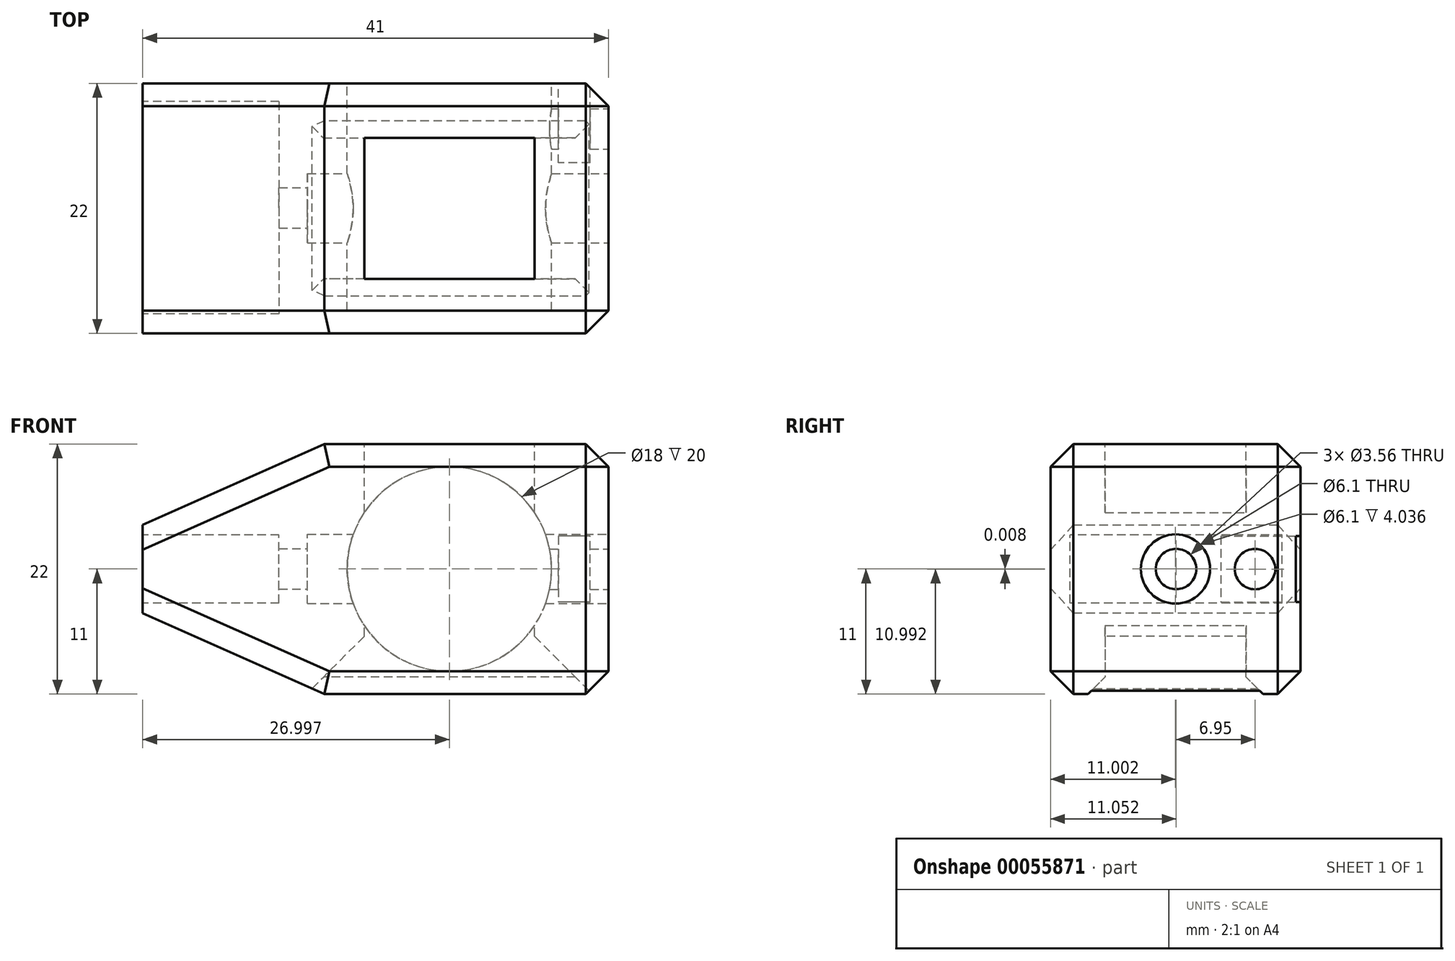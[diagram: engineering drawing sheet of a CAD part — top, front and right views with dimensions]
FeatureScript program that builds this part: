
annotation { "Feature Type Name" : "Feature", "Feature Type Description" : "" }
export const myFeature = defineFeature(function(context is Context, id is Id, definition is map)
    precondition{}
    {
        {
            var Q0;
            Q0=qCreatedBy(makeId("Top.planeOp"),FACE);
            var sketch = newSketch(context, id + "F0", { "sketchPlane" : qUnion([Q0])});
            skLineSegment(sketch, "E0.bottom", {"start": v(-13.98, 8.23) * mm, "end": v(12.02, 8.23) * mm});
            skLineSegment(sketch, "E0.top", {"start": v(-13.98, -13.77) * mm, "end": v(12.02, -13.77) * mm});
            skLineSegment(sketch, "E0.left", {"start": v(-13.98, 8.23) * mm, "end": v(-13.98, -13.77) * mm});
            skLineSegment(sketch, "E0.right", {"start": v(12.02, 8.23) * mm, "end": v(12.02, -13.77) * mm});
            skSolve(sketch);
        }
        {
            var Q0;
            Q0=qSketchRegion(id+"F0",true);
            extrude(context, id + "F1", {"entities" : qUnion([Q0]), "depth" : 22 * mm});
        }
        {
            var Q0;
            Q0=makeQuery(id+"F1.opExtrude","SWEPT_FACE",FACE,{"disambiguationData":[OSD([sQuery(id+"F0.wireOp",EDGE,"E0.bottom")])]});
            var sketch = newSketch(context, id + "F2", { "sketchPlane" : qUnion([Q0])});
            skCircle(sketch, "E1", {"center": v(0.98, 11) * mm, "radius": 9 * mm});
            skSolve(sketch);
        }
        {
            var Q0;
            Q0=qSketchRegion(id+"F2",true);
            extrude(context, id + "F3", {"entities" : qUnion([Q0]), "operationType" : NewBodyOperationType.REMOVE, "oppositeDirection" : true, "depth" : 20 * mm});
        }
        {
            var Q0;
            Q0=makeQuery(id+"F1.opExtrude","CAP_FACE",FACE,{"disambiguationData":[OSD([sQuery(id+"F0.wireOp",EDGE,"E0.bottom"),sQuery(id+"F0.wireOp",EDGE,"E0.top"),sQuery(id+"F0.wireOp",EDGE,"E0.left"),sQuery(id+"F0.wireOp",EDGE,"E0.right")])],"isStart":false});
            var sketch = newSketch(context, id + "F4", { "sketchPlane" : qUnion([Q0])});
            skLineSegment(sketch, "E2.bottom", {"start": v(-8.48, 3.43) * mm, "end": v(6.52, 3.43) * mm});
            skLineSegment(sketch, "E2.top", {"start": v(-8.48, -8.97) * mm, "end": v(6.52, -8.97) * mm});
            skLineSegment(sketch, "E2.left", {"start": v(-8.48, 3.43) * mm, "end": v(-8.48, -8.97) * mm});
            skLineSegment(sketch, "E2.right", {"start": v(6.52, 3.43) * mm, "end": v(6.52, -8.97) * mm});
            skSolve(sketch);
        }
        {
            var Q0;
            Q0=qSketchRegion(id+"F4",true);
            extrude(context, id + "F5", {"entities" : qUnion([Q0]), "operationType" : NewBodyOperationType.REMOVE, "endBound" : BoundingType.THROUGH_ALL, "oppositeDirection" : true, "depth" : 10 * mm});
        }
        {
            var Q0;
            Q0=makeQuery(id+"F1.opExtrude","SWEPT_FACE",FACE,{"disambiguationData":[OSD([sQuery(id+"F0.wireOp",EDGE,"E0.left")])]});
            var sketch = newSketch(context, id + "F6", { "sketchPlane" : qUnion([Q0])});
            skLineSegment(sketch, "E3.bottom", {"start": v(-8.23, 22) * mm, "end": v(13.77, 22) * mm});
            skLineSegment(sketch, "E3.top", {"start": v(-8.23, 0) * mm, "end": v(13.77, 0) * mm});
            skLineSegment(sketch, "E3.left", {"start": v(-8.23, 22) * mm, "end": v(-8.23, 0) * mm});
            skLineSegment(sketch, "E3.right", {"start": v(13.77, 22) * mm, "end": v(13.77, 0) * mm});
            skSolve(sketch);
        }
        {
            var Q0;
            Q0=qSketchRegion(id+"F6",true);
            extrude(context, id + "F7", {"entities" : qUnion([Q0]), "operationType" : NewBodyOperationType.ADD, "depth" : 14 * mm});
        }
        {
            var Q0;
            Q0=makeQuery(id+"F7.opExtrude","CAP_FACE",FACE,{"disambiguationData":[OSD([sQuery(id+"F6.wireOp",EDGE,"E3.bottom"),sQuery(id+"F6.wireOp",EDGE,"E3.top"),sQuery(id+"F6.wireOp",EDGE,"E3.left"),sQuery(id+"F6.wireOp",EDGE,"E3.right")])],"isStart":false});
            var sketch = newSketch(context, id + "F8", { "sketchPlane" : qUnion([Q0])});
            skLineSegment(sketch, "E4.bottom", {"start": v(-6.63, 8) * mm, "end": v(12.07, 8) * mm});
            skLineSegment(sketch, "E4.top", {"start": v(-6.63, 14) * mm, "end": v(12.07, 14) * mm});
            skLineSegment(sketch, "E4.left", {"start": v(-6.63, 8) * mm, "end": v(-6.63, 14) * mm});
            skLineSegment(sketch, "E4.right", {"start": v(12.07, 8) * mm, "end": v(12.07, 14) * mm});
            skSolve(sketch);
        }
        {
            var Q0;
            Q0=qSketchRegion(id+"F8",true);
            extrude(context, id + "F9", {"entities" : qUnion([Q0]), "operationType" : NewBodyOperationType.REMOVE, "oppositeDirection" : true, "depth" : 12 * mm});
        }
        {
            var Q0;
            Q0=makeQuery(id+"F1.opExtrude","SWEPT_FACE",FACE,{"disambiguationData":[OSD([sQuery(id+"F0.wireOp",EDGE,"E0.right")])]});
            var sketch = newSketch(context, id + "F10", { "sketchPlane" : qUnion([Q0])});
            skCircle(sketch, "E5", {"center": v(-2.72, 11) * mm, "radius": 1.78 * mm});
            skSolve(sketch);
        }
        {
            var Q0;
            Q0=qSketchRegion(id+"F10",true);
            extrude(context, id + "F11", {"entities" : qUnion([Q0]), "operationType" : NewBodyOperationType.REMOVE, "endBound" : BoundingType.THROUGH_ALL, "oppositeDirection" : true, "depth" : 25.4 * mm});
        }
        {
            var Q0;
            Q0=makeQuery(id+"F5.boolean.opBoolean","COPY",EDGE,{"derivedFrom":makeQuery(id+"F5.opExtrude","CAP_EDGE",EDGE,{"disambiguationData":[OSD([sQuery(id+"F4.wireOp",EDGE,"E2.bottom")])],"isStart":true})});
            var Q1;
            Q1=makeQuery(id+"F5.boolean.opBoolean","COPY",EDGE,{"derivedFrom":makeQuery(id+"F5.opExtrude","CAP_EDGE",EDGE,{"disambiguationData":[OSD([sQuery(id+"F4.wireOp",EDGE,"E2.top")])],"isStart":true})});
            var Q2;
            Q2=makeQuery(id+"F5.boolean.opBoolean","INTERSECT",EDGE,{"derivedFrom":[makeQuery(id+"F1.opExtrude","CAP_FACE",FACE,{"disambiguationData":[OSD([sQuery(id+"F0.wireOp",EDGE,"E0.bottom"),sQuery(id+"F0.wireOp",EDGE,"E0.top"),sQuery(id+"F0.wireOp",EDGE,"E0.left"),sQuery(id+"F0.wireOp",EDGE,"E0.right")])],"isStart":true}),makeQuery(id+"F5.opExtrude","SWEPT_FACE",FACE,{"disambiguationData":[OSD([sQuery(id+"F4.wireOp",EDGE,"E2.bottom")])]})]});
            var Q3;
            Q3=makeQuery(id+"F5.boolean.opBoolean","INTERSECT",EDGE,{"derivedFrom":[makeQuery(id+"F1.opExtrude","CAP_FACE",FACE,{"disambiguationData":[OSD([sQuery(id+"F0.wireOp",EDGE,"E0.bottom"),sQuery(id+"F0.wireOp",EDGE,"E0.top"),sQuery(id+"F0.wireOp",EDGE,"E0.left"),sQuery(id+"F0.wireOp",EDGE,"E0.right")])],"isStart":true}),makeQuery(id+"F5.opExtrude","SWEPT_FACE",FACE,{"disambiguationData":[OSD([sQuery(id+"F4.wireOp",EDGE,"E2.top")])]})]});
            chamfer(context, id + "F12", {"entities" : qUnion([Q0, Q1, Q2, Q3]), "width" : 1.5 * mm, "tangentPropagation" : true});
        }
        {
            var Q0;
            Q0=makeQuery(id+"F7.opExtrude","CAP_EDGE",EDGE,{"disambiguationData":[OSD([sQuery(id+"F6.wireOp",EDGE,"E3.bottom")])],"isStart":false});
            var Q1;
            Q1=makeQuery(id+"F7.opExtrude","CAP_EDGE",EDGE,{"disambiguationData":[OSD([sQuery(id+"F6.wireOp",EDGE,"E3.top")])],"isStart":false});
            chamfer(context, id + "F13", {"entities" : qUnion([Q0, Q1]), "chamferType" : ChamferType.OFFSET_ANGLE, "width" : 16 * mm, "oppositeDirection" : false, "angle" : 24 * degree, "tangentPropagation" : true});
        }
        {
            var Q0;
            Q0=makeQuery(id+"F13.opChamfer","BLEND_EDGE",EDGE,{"blendedFrom":[makeQuery(id+"F7.opExtrude","CAP_EDGE",EDGE,{"disambiguationData":[OSD([sQuery(id+"F6.wireOp",EDGE,"E3.bottom")])],"isStart":false}),makeQuery(id+"F7.boolean.opBoolean","MERGE",FACE,{"derivedFrom":[makeQuery(id+"F1.opExtrude","SWEPT_FACE",FACE,{"disambiguationData":[OSD([sQuery(id+"F0.wireOp",EDGE,"E0.bottom")])]}),makeQuery(id+"F7.opExtrude","SWEPT_FACE",FACE,{"disambiguationData":[OSD([sQuery(id+"F6.wireOp",EDGE,"E3.left")])]})]})],"blendedInto":[makeQuery(id+"F7.boolean.opBoolean","MERGE",FACE,{"derivedFrom":[makeQuery(id+"F1.opExtrude","SWEPT_FACE",FACE,{"disambiguationData":[OSD([sQuery(id+"F0.wireOp",EDGE,"E0.bottom")])]}),makeQuery(id+"F7.opExtrude","SWEPT_FACE",FACE,{"disambiguationData":[OSD([sQuery(id+"F6.wireOp",EDGE,"E3.left")])]})]})]});
            var Q1;
            Q1=makeQuery(id+"F13.opChamfer","BLEND_EDGE",EDGE,{"blendedFrom":[makeQuery(id+"F7.opExtrude","CAP_EDGE",EDGE,{"disambiguationData":[OSD([sQuery(id+"F6.wireOp",EDGE,"E3.bottom")])],"isStart":false}),makeQuery(id+"F7.boolean.opBoolean","MERGE",FACE,{"derivedFrom":[makeQuery(id+"F1.opExtrude","SWEPT_FACE",FACE,{"disambiguationData":[OSD([sQuery(id+"F0.wireOp",EDGE,"E0.top")])]}),makeQuery(id+"F7.opExtrude","SWEPT_FACE",FACE,{"disambiguationData":[OSD([sQuery(id+"F6.wireOp",EDGE,"E3.right")])]})]})],"blendedInto":[makeQuery(id+"F7.boolean.opBoolean","MERGE",FACE,{"derivedFrom":[makeQuery(id+"F1.opExtrude","SWEPT_FACE",FACE,{"disambiguationData":[OSD([sQuery(id+"F0.wireOp",EDGE,"E0.top")])]}),makeQuery(id+"F7.opExtrude","SWEPT_FACE",FACE,{"disambiguationData":[OSD([sQuery(id+"F6.wireOp",EDGE,"E3.right")])]})]})]});
            var Q2;
            Q2=makeQuery(id+"F13.opChamfer","BLEND_EDGE",EDGE,{"blendedFrom":[makeQuery(id+"F7.opExtrude","CAP_EDGE",EDGE,{"disambiguationData":[OSD([sQuery(id+"F6.wireOp",EDGE,"E3.top")])],"isStart":false}),makeQuery(id+"F7.boolean.opBoolean","MERGE",FACE,{"derivedFrom":[makeQuery(id+"F1.opExtrude","SWEPT_FACE",FACE,{"disambiguationData":[OSD([sQuery(id+"F0.wireOp",EDGE,"E0.bottom")])]}),makeQuery(id+"F7.opExtrude","SWEPT_FACE",FACE,{"disambiguationData":[OSD([sQuery(id+"F6.wireOp",EDGE,"E3.left")])]})]})],"blendedInto":[makeQuery(id+"F7.boolean.opBoolean","MERGE",FACE,{"derivedFrom":[makeQuery(id+"F1.opExtrude","SWEPT_FACE",FACE,{"disambiguationData":[OSD([sQuery(id+"F0.wireOp",EDGE,"E0.bottom")])]}),makeQuery(id+"F7.opExtrude","SWEPT_FACE",FACE,{"disambiguationData":[OSD([sQuery(id+"F6.wireOp",EDGE,"E3.left")])]})]})]});
            var Q3;
            Q3=makeQuery(id+"F13.opChamfer","BLEND_EDGE",EDGE,{"blendedFrom":[makeQuery(id+"F7.opExtrude","CAP_EDGE",EDGE,{"disambiguationData":[OSD([sQuery(id+"F6.wireOp",EDGE,"E3.top")])],"isStart":false}),makeQuery(id+"F7.boolean.opBoolean","MERGE",FACE,{"derivedFrom":[makeQuery(id+"F1.opExtrude","SWEPT_FACE",FACE,{"disambiguationData":[OSD([sQuery(id+"F0.wireOp",EDGE,"E0.top")])]}),makeQuery(id+"F7.opExtrude","SWEPT_FACE",FACE,{"disambiguationData":[OSD([sQuery(id+"F6.wireOp",EDGE,"E3.right")])]})]})],"blendedInto":[makeQuery(id+"F7.boolean.opBoolean","MERGE",FACE,{"derivedFrom":[makeQuery(id+"F1.opExtrude","SWEPT_FACE",FACE,{"disambiguationData":[OSD([sQuery(id+"F0.wireOp",EDGE,"E0.top")])]}),makeQuery(id+"F7.opExtrude","SWEPT_FACE",FACE,{"disambiguationData":[OSD([sQuery(id+"F6.wireOp",EDGE,"E3.right")])]})]})]});
            chamfer(context, id + "F14", {"entities" : qUnion([Q0, Q1, Q2, Q3]), "width" : 2 * mm, "tangentPropagation" : true});
        }
        {
            var Q0;
            Q0=makeQuery(id+"F14.opChamfer","SPLIT",FACE,{"disambiguationData":[OD(0.0)],"derivedFrom":makeQuery(id+"F7.boolean.opBoolean","MERGE",FACE,{"derivedFrom":[makeQuery(id+"F1.opExtrude","SWEPT_FACE",FACE,{"disambiguationData":[OSD([sQuery(id+"F0.wireOp",EDGE,"E0.bottom")])]}),makeQuery(id+"F7.opExtrude","SWEPT_FACE",FACE,{"disambiguationData":[OSD([sQuery(id+"F6.wireOp",EDGE,"E3.left")])]})]})});
            var sketch = newSketch(context, id + "F15", { "sketchPlane" : qUnion([Q0])});
            skLineSegment(sketch, "E6.bottom", {"start": v(-11.42, 13.9) * mm, "end": v(-8.62, 13.9) * mm});
            skLineSegment(sketch, "E6.top", {"start": v(-11.42, 8.1) * mm, "end": v(-8.62, 8.1) * mm});
            skLineSegment(sketch, "E6.left", {"start": v(-11.42, 13.9) * mm, "end": v(-11.42, 8.1) * mm});
            skLineSegment(sketch, "E6.right", {"start": v(-8.62, 13.9) * mm, "end": v(-8.62, 8.1) * mm});
            skSolve(sketch);
        }
        {
            var Q0;
            Q0=qSketchRegion(id+"F15",true);
            extrude(context, id + "F16", {"entities" : qUnion([Q0]), "operationType" : NewBodyOperationType.REMOVE, "oppositeDirection" : true, "depth" : 7 * mm});
        }
        {
            var Q0;
            Q0=makeQuery(id+"F1.opExtrude","SWEPT_FACE",FACE,{"disambiguationData":[OSD([sQuery(id+"F0.wireOp",EDGE,"E0.right")])]});
            var sketch = newSketch(context, id + "F17", { "sketchPlane" : qUnion([Q0])});
            skLineSegment(sketch, "E7.bottom", {"start": v(8.23, 22) * mm, "end": v(-13.77, 22) * mm});
            skLineSegment(sketch, "E7.top", {"start": v(8.23, 0) * mm, "end": v(-13.77, 0) * mm});
            skLineSegment(sketch, "E7.left", {"start": v(8.23, 22) * mm, "end": v(8.23, 0) * mm});
            skLineSegment(sketch, "E7.right", {"start": v(-13.77, 22) * mm, "end": v(-13.77, 0) * mm});
            skSolve(sketch);
        }
        {
            var Q0;
            Q0=qSketchRegion(id+"F17",true);
            extrude(context, id + "F18", {"entities" : qUnion([Q0]), "operationType" : NewBodyOperationType.ADD, "depth" : 1 * mm});
        }
        {
            var Q0;
            Q0=makeQuery(id+"F18.opExtrude","CAP_FACE",FACE,{"disambiguationData":[OSD([sQuery(id+"F17.wireOp",EDGE,"E7.bottom"),sQuery(id+"F17.wireOp",EDGE,"E7.top"),sQuery(id+"F17.wireOp",EDGE,"E7.left"),sQuery(id+"F17.wireOp",EDGE,"E7.right")])],"isStart":false});
            var sketch = newSketch(context, id + "F19", { "sketchPlane" : qUnion([Q0])});
            skCircle(sketch, "E8", {"center": v(-2.77, 11) * mm, "radius": 3.05 * mm});
            skSolve(sketch);
        }
        {
            var Q0;
            Q0=makeQuery(id+"F19.imprint","IMPRINT",FACE,{"disambiguationData":[TD([[makeQuery(id+"F19.imprint","IMPRINT",EDGE,{"derivedFrom":sQuery(id+"F19.wireOp",EDGE,"E8")}),1.0]])]});
            extrude(context, id + "F20", {"entities" : qUnion([Q0]), "operationType" : NewBodyOperationType.REMOVE, "oppositeDirection" : true, "depth" : 26.5 * mm});
        }
        {
            var Q0;
            Q0=makeQuery(id+"F18.opExtrude","CAP_FACE",FACE,{"disambiguationData":[OSD([sQuery(id+"F17.wireOp",EDGE,"E7.bottom"),sQuery(id+"F17.wireOp",EDGE,"E7.top"),sQuery(id+"F17.wireOp",EDGE,"E7.left"),sQuery(id+"F17.wireOp",EDGE,"E7.right")])],"isStart":false});
            var sketch = newSketch(context, id + "F21", { "sketchPlane" : qUnion([Q0])});
            skCircle(sketch, "E9", {"center": v(4.23, 11) * mm, "radius": 1.78 * mm});
            skSolve(sketch);
        }
        {
            var Q0;
            Q0=qSketchRegion(id+"F21",true);
            extrude(context, id + "F22", {"entities" : qUnion([Q0]), "operationType" : NewBodyOperationType.REMOVE, "oppositeDirection" : true, "depth" : 6 * mm});
        }
        {
            var Q0;
            Q0=makeQuery(id+"F18.opExtrude","CAP_EDGE",EDGE,{"disambiguationData":[OSD([sQuery(id+"F17.wireOp",EDGE,"E7.top")])],"isStart":false});
            var Q1;
            Q1=makeQuery(id+"F18.opExtrude","CAP_EDGE",EDGE,{"disambiguationData":[OSD([sQuery(id+"F17.wireOp",EDGE,"E7.left")])],"isStart":false});
            var Q2;
            Q2=makeQuery(id+"F18.opExtrude","CAP_EDGE",EDGE,{"disambiguationData":[OSD([sQuery(id+"F17.wireOp",EDGE,"E7.bottom")])],"isStart":false});
            var Q3;
            Q3=makeQuery(id+"F18.opExtrude","CAP_EDGE",EDGE,{"disambiguationData":[OSD([sQuery(id+"F17.wireOp",EDGE,"E7.right")])],"isStart":false});
            var Q4;
            Q4=makeQuery(id+"F18.boolean.opBoolean","MERGE",EDGE,{"derivedFrom":[makeQuery(id+"F7.boolean.opBoolean","MERGE",EDGE,{"derivedFrom":[makeQuery(id+"F1.opExtrude","CAP_EDGE",EDGE,{"disambiguationData":[OSD([sQuery(id+"F0.wireOp",EDGE,"E0.bottom")])],"isStart":false}),makeQuery(id+"F7.opExtrude","SWEPT_EDGE",EDGE,{"disambiguationData":[OSD([sQuery(id+"F6.wireOp",EDGE,"E3.bottom"),sQuery(id+"F6.wireOp",EDGE,"E3.left")])]})]}),makeQuery(id+"F18.opExtrude","SWEPT_EDGE",EDGE,{"disambiguationData":[OSD([sQuery(id+"F17.wireOp",EDGE,"E7.bottom"),sQuery(id+"F17.wireOp",EDGE,"E7.left")])]})]});
            var Q5;
            Q5=makeQuery(id+"F18.boolean.opBoolean","MERGE",EDGE,{"derivedFrom":[makeQuery(id+"F7.boolean.opBoolean","MERGE",EDGE,{"derivedFrom":[makeQuery(id+"F1.opExtrude","CAP_EDGE",EDGE,{"disambiguationData":[OSD([sQuery(id+"F0.wireOp",EDGE,"E0.top")])],"isStart":false}),makeQuery(id+"F7.opExtrude","SWEPT_EDGE",EDGE,{"disambiguationData":[OSD([sQuery(id+"F6.wireOp",EDGE,"E3.bottom"),sQuery(id+"F6.wireOp",EDGE,"E3.right")])]})]}),makeQuery(id+"F18.opExtrude","SWEPT_EDGE",EDGE,{"disambiguationData":[OSD([sQuery(id+"F17.wireOp",EDGE,"E7.bottom"),sQuery(id+"F17.wireOp",EDGE,"E7.right")])]})]});
            var Q6;
            Q6=makeQuery(id+"F18.boolean.opBoolean","MERGE",EDGE,{"derivedFrom":[makeQuery(id+"F7.boolean.opBoolean","MERGE",EDGE,{"derivedFrom":[makeQuery(id+"F1.opExtrude","CAP_EDGE",EDGE,{"disambiguationData":[OSD([sQuery(id+"F0.wireOp",EDGE,"E0.top")])],"isStart":true}),makeQuery(id+"F7.opExtrude","SWEPT_EDGE",EDGE,{"disambiguationData":[OSD([sQuery(id+"F6.wireOp",EDGE,"E3.top"),sQuery(id+"F6.wireOp",EDGE,"E3.right")])]})]}),makeQuery(id+"F18.opExtrude","SWEPT_EDGE",EDGE,{"disambiguationData":[OSD([sQuery(id+"F17.wireOp",EDGE,"E7.top"),sQuery(id+"F17.wireOp",EDGE,"E7.right")])]})]});
            var Q7;
            Q7=makeQuery(id+"F18.boolean.opBoolean","MERGE",EDGE,{"derivedFrom":[makeQuery(id+"F7.boolean.opBoolean","MERGE",EDGE,{"derivedFrom":[makeQuery(id+"F1.opExtrude","CAP_EDGE",EDGE,{"disambiguationData":[OSD([sQuery(id+"F0.wireOp",EDGE,"E0.bottom")])],"isStart":true}),makeQuery(id+"F7.opExtrude","SWEPT_EDGE",EDGE,{"disambiguationData":[OSD([sQuery(id+"F6.wireOp",EDGE,"E3.top"),sQuery(id+"F6.wireOp",EDGE,"E3.left")])]})]}),makeQuery(id+"F18.opExtrude","SWEPT_EDGE",EDGE,{"disambiguationData":[OSD([sQuery(id+"F17.wireOp",EDGE,"E7.top"),sQuery(id+"F17.wireOp",EDGE,"E7.left")])]})]});
            chamfer(context, id + "F23", {"entities" : qUnion([Q0, Q1, Q2, Q3, Q4, Q5, Q6, Q7]), "width" : 2 * mm, "tangentPropagation" : true});
        }
        {
            var Q0;
            Q0=makeQuery(id+"F5.boolean.opBoolean","COPY",EDGE,{"derivedFrom":makeQuery(id+"F5.opExtrude","CAP_EDGE",EDGE,{"disambiguationData":[OSD([sQuery(id+"F4.wireOp",EDGE,"E2.left")])],"isStart":true})});
            var Q1;
            Q1=makeQuery(id+"F5.boolean.opBoolean","COPY",EDGE,{"derivedFrom":makeQuery(id+"F5.opExtrude","CAP_EDGE",EDGE,{"disambiguationData":[OSD([sQuery(id+"F4.wireOp",EDGE,"E2.right")])],"isStart":true})});
            var Q2;
            Q2=makeQuery(id+"F5.boolean.opBoolean","INTERSECT",EDGE,{"derivedFrom":[makeQuery(id+"F1.opExtrude","CAP_FACE",FACE,{"disambiguationData":[OSD([sQuery(id+"F0.wireOp",EDGE,"E0.bottom"),sQuery(id+"F0.wireOp",EDGE,"E0.top"),sQuery(id+"F0.wireOp",EDGE,"E0.left"),sQuery(id+"F0.wireOp",EDGE,"E0.right")])],"isStart":true}),makeQuery(id+"F5.opExtrude","SWEPT_FACE",FACE,{"disambiguationData":[OSD([sQuery(id+"F4.wireOp",EDGE,"E2.right")])]})]});
            var Q3;
            Q3=makeQuery(id+"F5.boolean.opBoolean","INTERSECT",EDGE,{"derivedFrom":[makeQuery(id+"F1.opExtrude","CAP_FACE",FACE,{"disambiguationData":[OSD([sQuery(id+"F0.wireOp",EDGE,"E0.bottom"),sQuery(id+"F0.wireOp",EDGE,"E0.top"),sQuery(id+"F0.wireOp",EDGE,"E0.left"),sQuery(id+"F0.wireOp",EDGE,"E0.right")])],"isStart":true}),makeQuery(id+"F5.opExtrude","SWEPT_FACE",FACE,{"disambiguationData":[OSD([sQuery(id+"F4.wireOp",EDGE,"E2.left")])]})]});
            chamfer(context, id + "F24", {"entities" : qUnion([Q0, Q1, Q2, Q3]), "width" : 5.08 * mm, "tangentPropagation" : true});
        }
    });
